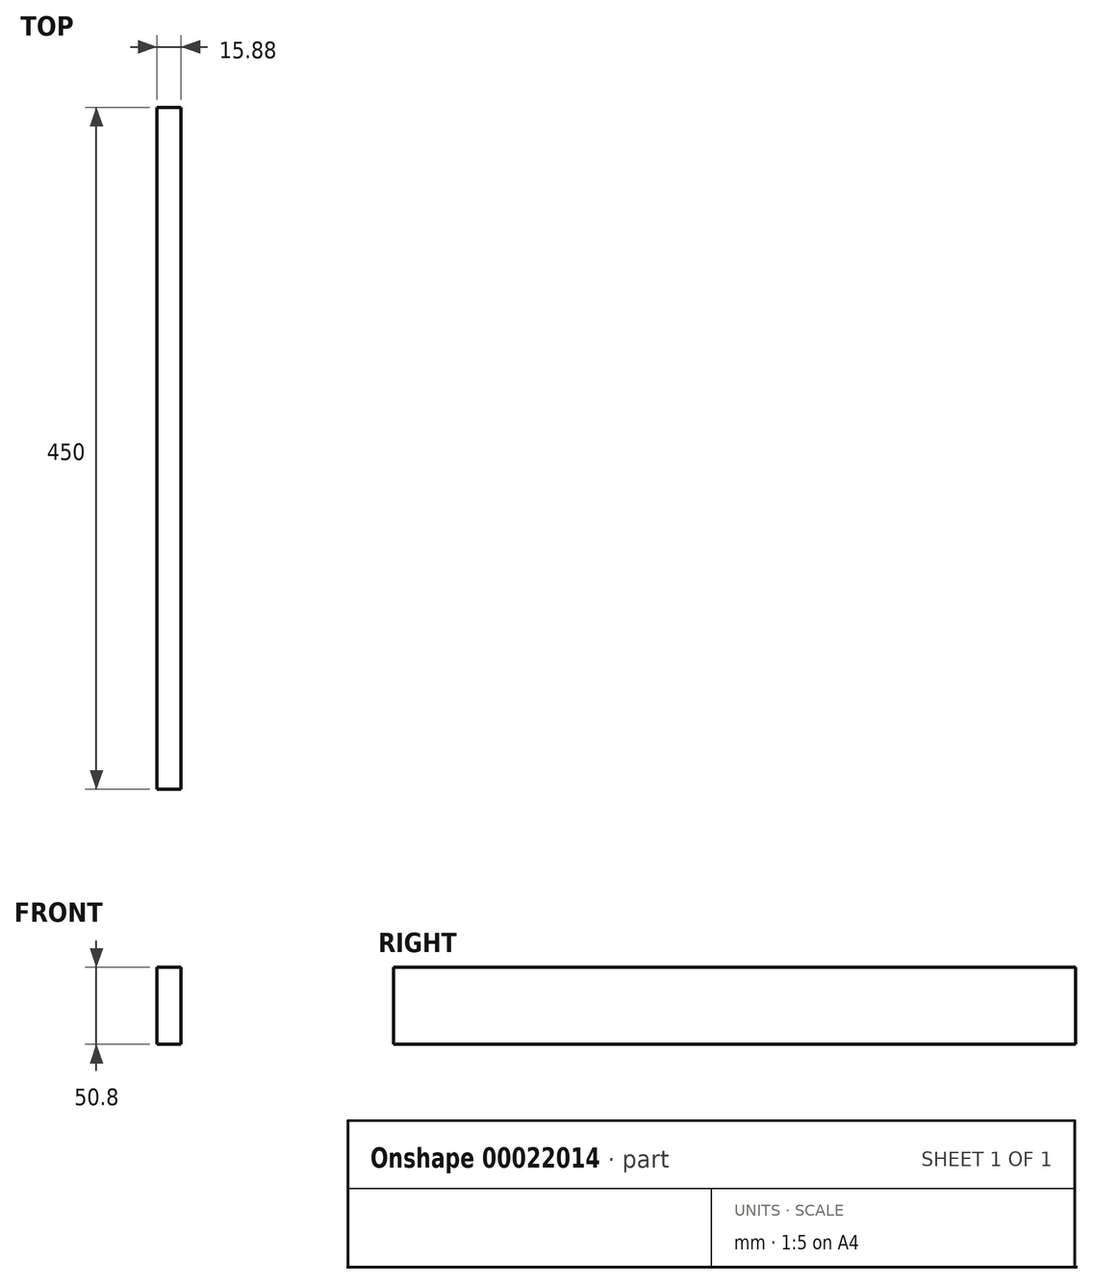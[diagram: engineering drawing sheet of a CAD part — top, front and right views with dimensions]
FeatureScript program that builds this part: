
annotation { "Feature Type Name" : "Feature", "Feature Type Description" : "" }
export const myFeature = defineFeature(function(context is Context, id is Id, definition is map)
    precondition{}
    {
        {
            var Q0;
            Q0=qCreatedBy(makeId("Top.planeOp"),FACE);
            var sketch = newSketch(context, id + "F0", { "sketchPlane" : qUnion([Q0])});
            skLineSegment(sketch, "E0.bottom", {"start": v(0, 0) * mm, "end": v(-15.88, 0) * mm});
            skLineSegment(sketch, "E0.top", {"start": v(0, -450) * mm, "end": v(-15.87, -450) * mm});
            skLineSegment(sketch, "E0.left", {"start": v(0, 0) * mm, "end": v(0, -450) * mm});
            skLineSegment(sketch, "E0.right", {"start": v(-15.88, 0) * mm, "end": v(-15.88, -450) * mm});
            skSolve(sketch);
        }
        {
            var Q0;
            Q0 = qSketchRegion(id + "F0", true);
            extrude(context, id + "F1", {"entities" : qUnion([Q0]), "depth" : 50.8 * mm});
        }
    });
